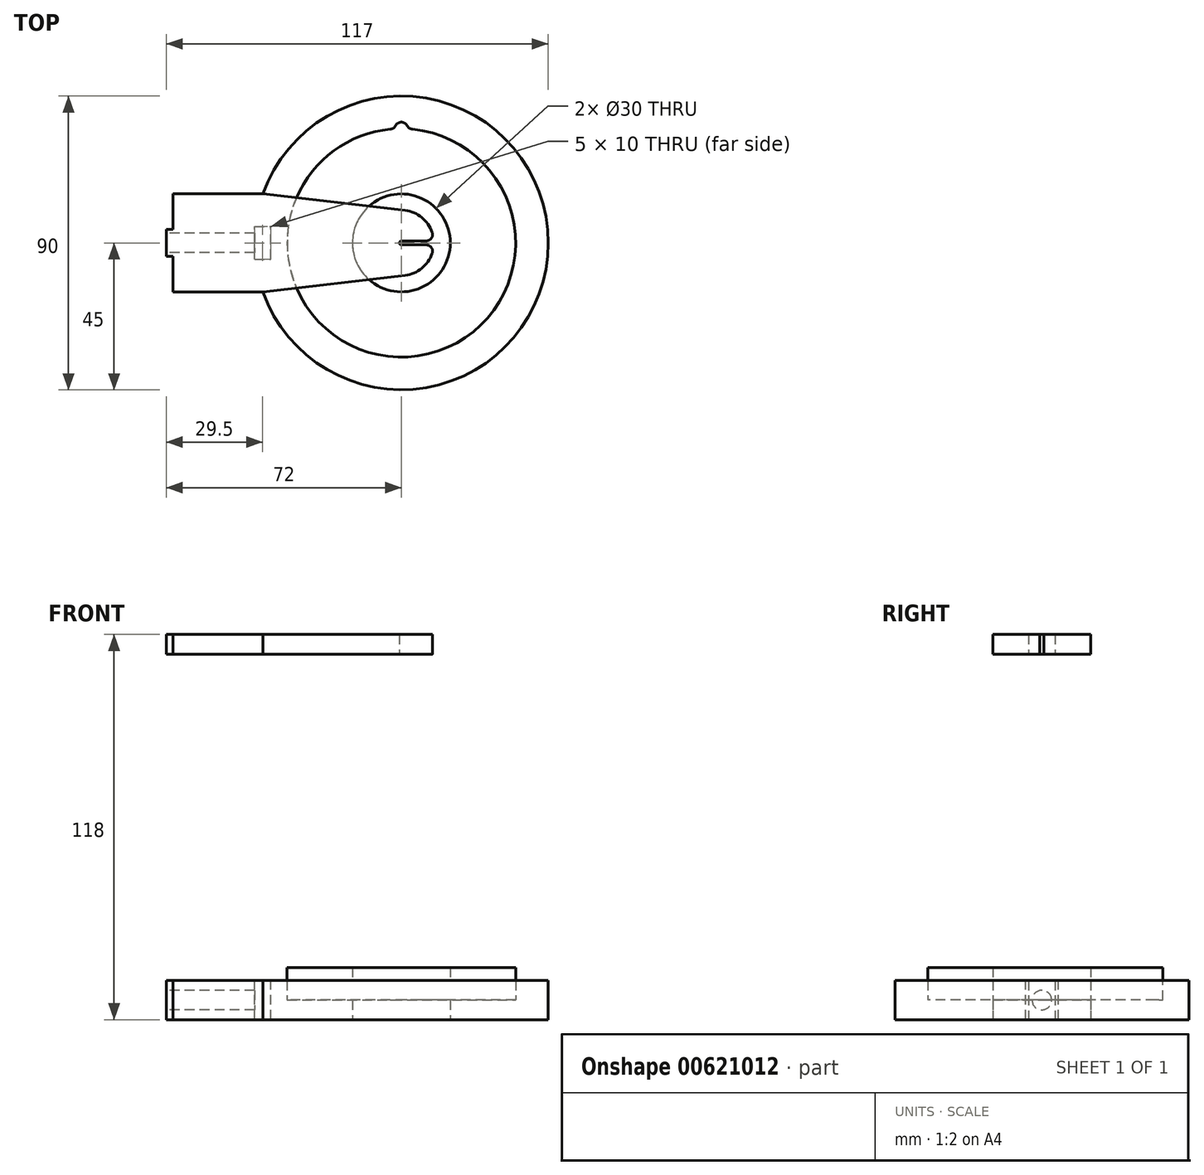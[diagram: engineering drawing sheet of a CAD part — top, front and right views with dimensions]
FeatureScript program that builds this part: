
annotation { "Feature Type Name" : "Feature", "Feature Type Description" : "" }
export const myFeature = defineFeature(function(context is Context, id is Id, definition is map)
    precondition{}
    {
        {
            var Q0;
            Q0=qCreatedBy(makeId("Top.planeOp"),FACE);
            var sketch = newSketch(context, id + "F0", { "sketchPlane" : qUnion([Q0])});
            skCircle(sketch, "E0", {"center": v(0, 0) * mm, "radius": 15 * mm});
            skCircle(sketch, "E1", {"center": v(0, 0) * mm, "radius": 35 * mm});
            skCircle(sketch, "E2", {"center": v(0, 0) * mm, "radius": 45 * mm});
            skLineSegment(sketch, "E3", {"start": v(-42.43, 15) * mm, "end": v(-70, 15) * mm});
            skLineSegment(sketch, "E4", {"start": v(-70, 15) * mm, "end": v(-70, -15) * mm});
            skLineSegment(sketch, "E5", {"start": v(-70, -15) * mm, "end": v(-42.43, -15) * mm});
            skSolve(sketch);
        }
        {
            var Q0;
            Q0=makeQuery(id+"F0.imprint","IMPRINT",FACE,{"disambiguationData":[TD([[makeQuery(id+"F0.imprint","IMPRINT",EDGE,{"derivedFrom":sQuery(id+"F0.wireOp",EDGE,"E0")}),-1.0]])]});
            extrude(context, id + "F1", {"entities" : qUnion([Q0]), "depth" : 6 * mm, "offsetDistance" : 25 * mm});
        }
        {
            var Q0;
            Q0=makeQuery(id+"F0.imprint","IMPRINT",FACE,{"disambiguationData":[TD([[makeQuery(id+"F0.imprint","IMPRINT",EDGE,{"derivedFrom":sQuery(id+"F0.wireOp",EDGE,"E1")}),-1.0]])]});
            var Q1;
            {var subQ0=sQuery(id+"F0.wireOp",EDGE,"E3");Q1=makeQuery(id+"F0.imprint","IMPRINT",FACE,{"disambiguationData":[TD([[makeQuery(id+"F0.imprint","IMPRINT",EDGE,{"derivedFrom":subQ0}),1.0]])]});}
            extrude(context, id + "F2", {"entities" : qUnion([Q0, Q1]), "operationType" : NewBodyOperationType.ADD, "depth" : 12 * mm, "offsetDistance" : 25 * mm});
        }
        {
            var Q0;
            Q0=makeQuery(id+"F2.opExtrude","CAP_FACE",FACE,{"disambiguationData":[OSD([sQuery(id+"F0.wireOp",EDGE,"E1"),sQuery(id+"F0.wireOp",EDGE,"E2"),sQuery(id+"F0.wireOp",EDGE,"E3"),sQuery(id+"F0.wireOp",EDGE,"E4"),sQuery(id+"F0.wireOp",EDGE,"E5")])],"isStart":false});
            var sketch = newSketch(context, id + "F3", { "sketchPlane" : qUnion([Q0])});
            skCircle(sketch, "E6", {"center": v(0, 35) * mm, "radius": 2 * mm});
            skSolve(sketch);
        }
        {
            var Q0;
            Q0=qSketchRegion(id+"F3",true);
            var Q1;
            Q1=makeQuery(id+"F1.opExtrude","CAP_FACE",FACE,{"disambiguationData":[OSD([sQuery(id+"F0.wireOp",EDGE,"E0"),sQuery(id+"F0.wireOp",EDGE,"E1")])],"isStart":false});
            extrude(context, id + "F4", {"entities" : qUnion([Q0]), "operationType" : NewBodyOperationType.REMOVE, "endBound" : BoundingType.UP_TO_SURFACE, "oppositeDirection" : true, "depth" : 5 * mm, "endBoundEntityFace" : qUnion([Q1]), "offsetDistance" : 25 * mm});
        }
        {
            var Q0;
            Q0=makeQuery(id+"F4.boolean.opBoolean","INTERSECT",EDGE,{"disambiguationData":[OD(0.0)],"derivedFrom":[makeQuery(id+"F2.opExtrude","SWEPT_FACE",FACE,{"disambiguationData":[OSD([sQuery(id+"F0.wireOp",EDGE,"E1")])]}),makeQuery(id+"F4.opExtrude","SWEPT_FACE",FACE,{"disambiguationData":[OSD([sQuery(id+"F3.wireOp",EDGE,"E6")])]})]});
            var Q1;
            Q1=makeQuery(id+"F4.boolean.opBoolean","INTERSECT",EDGE,{"disambiguationData":[OD(1.0)],"derivedFrom":[makeQuery(id+"F2.opExtrude","SWEPT_FACE",FACE,{"disambiguationData":[OSD([sQuery(id+"F0.wireOp",EDGE,"E1")])]}),makeQuery(id+"F4.opExtrude","SWEPT_FACE",FACE,{"disambiguationData":[OSD([sQuery(id+"F3.wireOp",EDGE,"E6")])]})]});
            fillet(context, id + "F5", {"entities" : qUnion([Q0, Q1]), "radius" : 2 * mm, "tangentPropagation" : true, "allowEdgeOverflow" : false});
        }
        {
            var Q0;
            Q0=makeQuery(id+"F2.opExtrude","CAP_FACE",FACE,{"disambiguationData":[OSD([sQuery(id+"F0.wireOp",EDGE,"E1"),sQuery(id+"F0.wireOp",EDGE,"E2"),sQuery(id+"F0.wireOp",EDGE,"E3"),sQuery(id+"F0.wireOp",EDGE,"E4"),sQuery(id+"F0.wireOp",EDGE,"E5")])],"isStart":false});
            var sketch = newSketch(context, id + "F6", { "sketchPlane" : qUnion([Q0])});
            skLineSegment(sketch, "E7.bottom", {"start": v(-40, 5) * mm, "end": v(-45, 5) * mm});
            skLineSegment(sketch, "E7.top", {"start": v(-40, -5) * mm, "end": v(-45, -5) * mm});
            skLineSegment(sketch, "E7.left", {"start": v(-40, 5) * mm, "end": v(-40, -5) * mm});
            skLineSegment(sketch, "E7.right", {"start": v(-45, 5) * mm, "end": v(-45, -5) * mm});
            skPoint(sketch, "E7.middle", {"position": v(-42.5, 0) * mm});
            skSolve(sketch);
        }
        {
            var Q0;
            Q0=qSketchRegion(id+"F6",true);
            extrude(context, id + "F7", {"entities" : qUnion([Q0]), "operationType" : NewBodyOperationType.REMOVE, "endBound" : BoundingType.UP_TO_NEXT, "oppositeDirection" : true, "depth" : 25 * mm, "offsetDistance" : 25 * mm});
        }
        {
            var Q0;
            Q0=makeQuery(id+"F2.opExtrude","SWEPT_FACE",FACE,{"disambiguationData":[OSD([sQuery(id+"F0.wireOp",EDGE,"E4")])]});
            var sketch = newSketch(context, id + "F8", { "sketchPlane" : qUnion([Q0])});
            skLineSegment(sketch, "E8", {"start": v(0, 12) * mm, "end": v(0, 0) * mm, "construction": true});
            skLineSegment(sketch, "E9.bottom", {"start": v(4.1, 12) * mm, "end": v(-4.1, 12) * mm});
            skLineSegment(sketch, "E9.top", {"start": v(4.1, 0) * mm, "end": v(-4.1, 0) * mm});
            skLineSegment(sketch, "E9.left", {"start": v(4.1, 12) * mm, "end": v(4.1, 0) * mm});
            skLineSegment(sketch, "E9.right", {"start": v(-4.1, 12) * mm, "end": v(-4.1, 0) * mm});
            skPoint(sketch, "E9.middle", {"position": v(0, 6) * mm});
            skSolve(sketch);
        }
        {
            var Q0;
            Q0=makeQuery(id+"F8.imprint","IMPRINT",FACE,{"disambiguationData":[TD([[makeQuery(id+"F8.imprint","IMPRINT",EDGE,{"derivedFrom":sQuery(id+"F8.wireOp",EDGE,"E9.bottom")}),-1.0]])]});
            extrude(context, id + "F9", {"entities" : qUnion([Q0]), "operationType" : NewBodyOperationType.ADD, "depth" : 2 * mm, "offsetDistance" : 25 * mm});
        }
        {
            var Q0;
            Q0=makeQuery(id+"F6.imprint","IMPRINT",FACE,{"disambiguationData":[TD([[makeQuery(id+"F6.imprint","IMPRINT",EDGE,{"derivedFrom":sQuery(id+"F6.wireOp",EDGE,"E7.bottom")}),-1.0]])]});
            var sketch = newSketch(context, id + "F10", { "sketchPlane" : qUnion([Q0])});
            skLineSegment(sketch, "E10.0.0", {"start": v(-70, -15) * mm, "end": v(-42.43, -15) * mm});
            skArc(sketch, "E10.0.1", {"start": v(-42.43, -15) * mm, "mid": v(45, 0) * mm, "end": v(-42.43, 15) * mm});
            skLineSegment(sketch, "E10.0.2", {"start": v(-42.43, 15) * mm, "end": v(-70, 15) * mm});
            skLineSegment(sketch, "E10.0.3", {"start": v(-70, 15) * mm, "end": v(-70, -15) * mm});
            skCircle(sketch, "E11.0", {"center": v(0, 0) * mm, "radius": 15 * mm});
            skSolve(sketch);
        }
        {
            var Q0;
            Q0=makeQuery(id+"F10.imprint","IMPRINT",FACE,{"disambiguationData":[TD([[makeQuery(id+"F10.imprint","IMPRINT",EDGE,{"derivedFrom":sQuery(id+"F10.wireOp",EDGE,"E11.0")}),-1.0]])]});
            extrude(context, id + "F11", {"entities" : qUnion([Q0]), "depth" : 4 * mm, "offsetDistance" : 25 * mm});
        }
        {
            var Q0;
            Q0=makeQuery(id+"F9.boolean.opBoolean","MERGE",FACE,{"derivedFrom":[makeQuery(id+"F2.opExtrude","CAP_FACE",FACE,{"disambiguationData":[OSD([sQuery(id+"F0.wireOp",EDGE,"E1"),sQuery(id+"F0.wireOp",EDGE,"E2"),sQuery(id+"F0.wireOp",EDGE,"E3"),sQuery(id+"F0.wireOp",EDGE,"E4"),sQuery(id+"F0.wireOp",EDGE,"E5")])],"isStart":false}),makeQuery(id+"F9.opExtrude","SWEPT_FACE",FACE,{"disambiguationData":[OSD([sQuery(id+"F8.wireOp",EDGE,"E9.bottom")])]})]});
            cPlane(context, id + "F12", {"entities" : qUnion([Q0]), "cplaneType" : CPlaneType.OFFSET, "offset" : 100 * mm, "width" : 150 * mm, "height" : 150 * mm});
        }
        {
            var Q0;
            Q0=qCreatedBy(id+"F12.planeOp",FACE);
            var sketch = newSketch(context, id + "F13", { "sketchPlane" : qUnion([Q0])});
            skCircle(sketch, "E12", {"center": v(0, 0) * mm, "radius": 0.6 * mm});
            skArc(sketch, "E13", {"start": v(9.46, 3.25) * mm, "mid": v(-10, 0) * mm, "end": v(9.46, -3.25) * mm});
            skLineSegment(sketch, "E14.0", {"start": v(-42.43, 15) * mm, "end": v(-70, 15) * mm});
            skLineSegment(sketch, "E15.0", {"start": v(-70, 15) * mm, "end": v(-70, 4.1) * mm});
            skLineSegment(sketch, "E16.0", {"start": v(-72, 4.1) * mm, "end": v(-70, 4.1) * mm});
            skLineSegment(sketch, "E17.0", {"start": v(-72, 4.1) * mm, "end": v(-72, -4.1) * mm});
            skLineSegment(sketch, "E18.0", {"start": v(-72, -4.1) * mm, "end": v(-70, -4.1) * mm});
            skLineSegment(sketch, "E19.0", {"start": v(-70, -4.1) * mm, "end": v(-70, -15) * mm});
            skLineSegment(sketch, "E20.0", {"start": v(-70, -15) * mm, "end": v(-42.43, -15) * mm});
            skLineSegment(sketch, "E21", {"start": v(-42.43, 15) * mm, "end": v(1.15, 9.93) * mm});
            skLineSegment(sketch, "E22", {"start": v(-42.43, -15) * mm, "end": v(1.15, -9.93) * mm});
            skLineSegment(sketch, "E23", {"start": v(7.57, 0.6) * mm, "end": v(0, 0.6) * mm});
            skLineSegment(sketch, "E24.MirrorCS", {"start": v(7.57, -0.6) * mm, "end": v(0, -0.6) * mm});
            skPoint(sketch, "E25.visualSharp", {"position": v(9.98, 0.6) * mm});
            skArc(sketch, "E25.filletArc", {"start": v(7.57, 0.6) * mm, "mid": v(9.2, 1.44) * mm, "end": v(9.46, 3.25) * mm});
            skPoint(sketch, "E26.visualSharp", {"position": v(9.98, -0.6) * mm});
            skArc(sketch, "E26.filletArc", {"start": v(9.46, -3.25) * mm, "mid": v(9.2, -1.44) * mm, "end": v(7.57, -0.6) * mm});
            skSolve(sketch);
        }
        {
            var Q0;
            Q0=makeQuery(id+"F13.imprint","IMPRINT",FACE,{"disambiguationData":[TD([[makeQuery(id+"F13.imprint","IMPRINT",EDGE,{"derivedFrom":sQuery(id+"F13.wireOp",EDGE,"E14.0")}),1.0]])]});
            var Q1;
            {var subQ5=sQuery(id+"F13.wireOp",EDGE,"E23");Q1=makeQuery(id+"F13.imprint","IMPRINT",FACE,{"disambiguationData":[TD([[makeQuery(id+"F13.imprint","IMPRINT",EDGE,{"derivedFrom":subQ5}),-1.0]])]});}
            extrude(context, id + "F14", {"entities" : qUnion([Q0, Q1]), "depth" : 6 * mm, "offsetDistance" : 25 * mm});
        }
        {
            var Q0;
            Q0=makeQuery(id+"F9.opExtrude","CAP_FACE",FACE,{"disambiguationData":[OSD([sQuery(id+"F8.wireOp",EDGE,"E9.bottom"),sQuery(id+"F8.wireOp",EDGE,"E9.top"),sQuery(id+"F8.wireOp",EDGE,"E9.left"),sQuery(id+"F8.wireOp",EDGE,"E9.right")])],"isStart":false});
            var sketch = newSketch(context, id + "F15", { "sketchPlane" : qUnion([Q0])});
            skCircle(sketch, "E27", {"center": v(0, 6) * mm, "radius": 3 * mm});
            skPoint(sketch, "E27.centerSnap0", {"position": v(4.1, 6) * mm});
            skSolve(sketch);
        }
        {
            var Q0;
            Q0 = qSketchRegion(id + "F15", true);
            extrude(context, id + "F16", {"entities" : qUnion([Q0]), "operationType" : NewBodyOperationType.REMOVE, "endBound" : BoundingType.UP_TO_NEXT, "oppositeDirection" : true, "depth" : 25 * mm, "offsetDistance" : 25 * mm});
        }
    });
